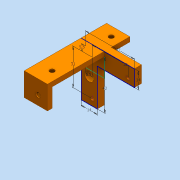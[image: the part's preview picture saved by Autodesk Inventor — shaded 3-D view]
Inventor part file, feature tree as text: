
AUTODESK INVENTOR PART (.ipt)
format: ipt  version: 2016 (Build 200138000, 138)  size: 231,424 bytes
history: native  units: mm
features: extrude x9, sketch x9, hole x7
ambient origin geometry x8: Origin, YZ Plane, XZ Plane, XY Plane, X Axis, Y Axis, Z Axis, Center Point
bodies: Solid1 (feature_tree)
feature tree (25):
  extrude  "Extrusion1"  Depth=20.0mm
  extrude  "Extrusion2"  Depth=45.0mm TaperAngle=0.0deg
  hole  "Hole2"  [1 undecoded]
  hole  "Hole3"  [1 undecoded]
  hole  "Hole4"  [1 undecoded]
  sketch  "Sketch3"  dims[d15=37.0mm d16=8.0mm d17=4.0mm d18=6.0mm d19=8.0mm d20=2.0mm d21=90.0deg d22=8.0mm d23=20.594885mm]
  sketch  "Sketch4"  dims[d24=37.0mm d25=8.0mm d26=4.0mm d27=6.0mm d28=8.0mm d29=2.0mm d30=90.0deg d31=8.0mm d32=20.594885mm]
  sketch  "Sketch5"  dims[d33=8.0mm d34=8.0mm d35=4.0mm d36=6.0mm d37=8.0mm d38=2.0mm d39=90.0deg d40=8.0mm d41=20.594885mm d51=7.0mm]
  extrude  "Extrusion3"  Depth=14.0mm
  extrude  "Extrusion4"  Depth=42.0mm
  extrude  "Extrusion5"  Depth=5.5mm
  sketch  "Sketch6"  dims[d52=7.0mm d53=7.0mm]
  extrude  "Extrusion6"  Depth=5.5mm
  hole  "Hole5"  [1 undecoded]
  extrude  "Extrusion7"  Depth=2.0mm
  hole  "Hole6"  [1 undecoded]
  hole  "Hole7"  [1 undecoded]
  sketch  "Sketch8"  dims[d58=3.2mm d59=0.0mm d62=14.0mm]
  extrude  "Extrusion8"  Depth=20.0mm
  extrude  "Extrusion9"  Depth=4.0mm
  hole  "Hole8"  [1 undecoded]
  sketch  "Sketch1"  dims[d0=20.0mm d1=20.0mm]
  sketch  "Sketch2"  dims[d2=4.0mm d3=0.0mm d4=45.0mm d5=0.0mm]
  sketch  "Sketch7"  dims[d54=3.2mm d55=0.0mm d56=3.2mm d57=0.0mm]
  sketch  "Sketch9"  dims[d65=42.0mm d66=42.0mm d68=5.5mm d69=5.5mm d70=31.0mm d71=31.0mm d72=14.0mm d73=6.0mm d74=0.0mm d75=3.0mm d76=6.0mm d77=4.0mm d78=2.0mm d79=90.0deg d80=8.0mm d81=20.594885mm d82=20.0mm d83=4.0mm d84=4.0mm d85=20.0mm d86=16.0mm d87=0.0mm d88=8.0mm d89=8.0mm d90=4.0mm d91=6.0mm d92=4.0mm d93=2.0mm d94=90.0deg d95=8.0mm d96=20.594885mm d97=8.0mm d98=8.0mm d99=4.0mm d100=6.0mm d101=4.0mm d102=2.0mm d103=90.0deg d104=8.0mm d105=20.594885mm d106=7.0mm d107=7.0mm d108=3.2mm d109=0.0mm d110=3.2mm d111=0.0mm d112=7.0mm d113=25.0mm d114=8.0mm d115=6.0mm d116=4.0mm d117=2.0mm d118=90.0deg d119=8.0mm d120=20.594885mm]
note: 7 required parameter values undecoded (feature->parameter linkage not recoverable at this tier; creation-order binding heuristic only, values carry confidence <= 0.55)
